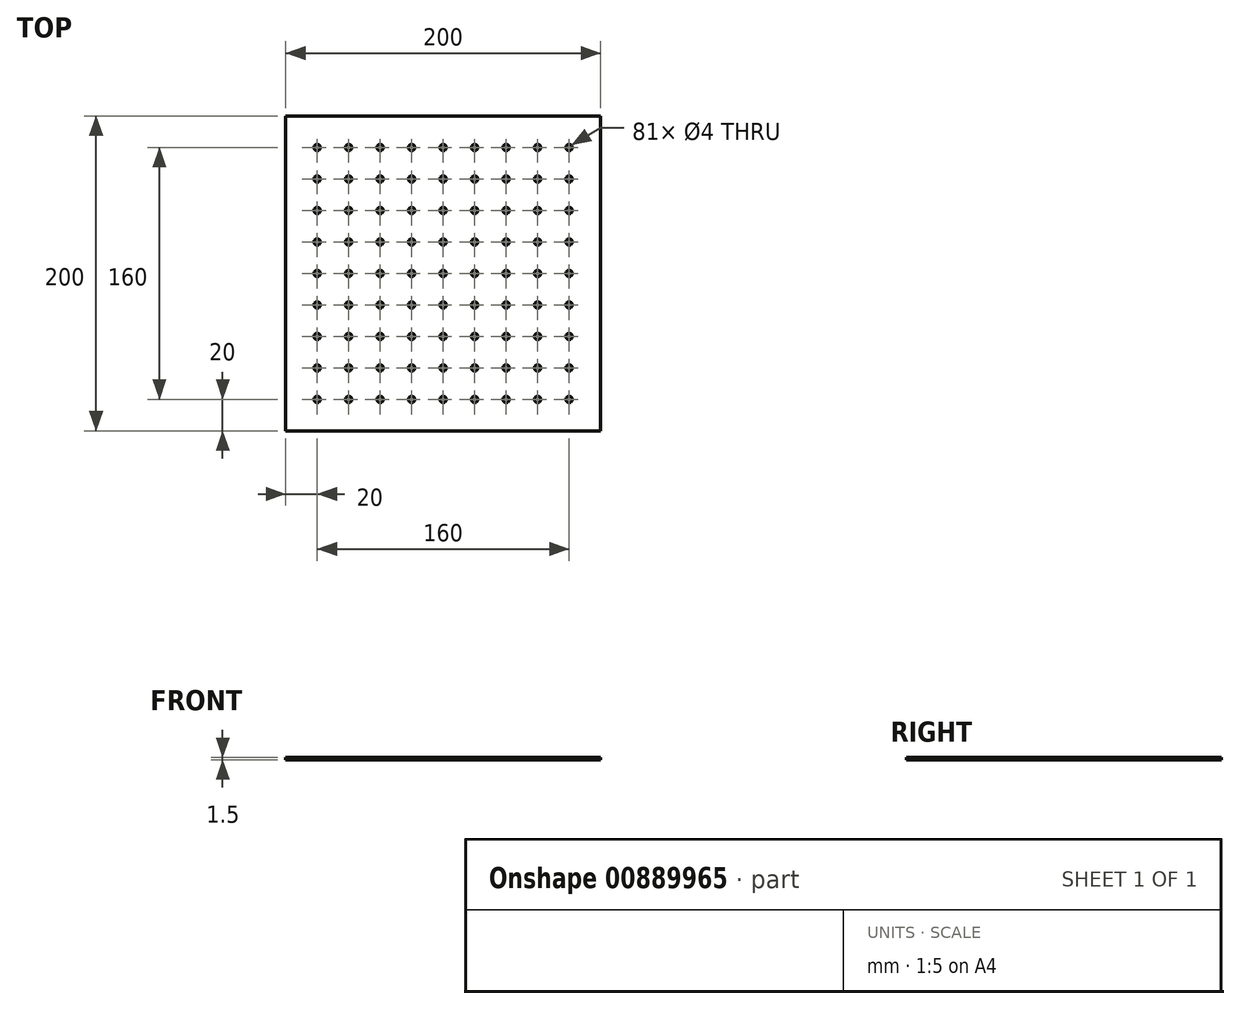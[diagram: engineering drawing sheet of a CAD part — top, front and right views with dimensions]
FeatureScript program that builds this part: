
annotation { "Feature Type Name" : "Feature", "Feature Type Description" : "" }
export const myFeature = defineFeature(function(context is Context, id is Id, definition is map)
    precondition{}
    {
        {
            var Q0;
            Q0=qCreatedBy(makeId("Top.planeOp"),FACE);
            var sketch = newSketch(context, id + "F0", { "sketchPlane" : qUnion([Q0])});
            skLineSegment(sketch, "E0.bottom", {"start": v(-100, 100) * mm, "end": v(100, 100) * mm});
            skLineSegment(sketch, "E0.top", {"start": v(-100, -100) * mm, "end": v(100, -100) * mm});
            skLineSegment(sketch, "E0.left", {"start": v(-100, 100) * mm, "end": v(-100, -100) * mm});
            skLineSegment(sketch, "E0.right", {"start": v(100, 100) * mm, "end": v(100, -100) * mm});
            skPoint(sketch, "E0.middle", {"position": v(0, 0) * mm});
            skCircle(sketch, "E1", {"center": v(-80, -80) * mm, "radius": 2 * mm});
            skCircle(sketch, "E2.0.1.0", {"center": v(-80, -60) * mm, "radius": 2 * mm});
            skCircle(sketch, "E2.0.2.0", {"center": v(-80, -40) * mm, "radius": 2 * mm});
            skCircle(sketch, "E2.0.3.0", {"center": v(-80, -20) * mm, "radius": 2 * mm});
            skCircle(sketch, "E2.0.4.0", {"center": v(-80, 0) * mm, "radius": 2 * mm});
            skCircle(sketch, "E2.0.5.0", {"center": v(-80, 20) * mm, "radius": 2 * mm});
            skCircle(sketch, "E2.0.6.0", {"center": v(-80, 40) * mm, "radius": 2 * mm});
            skCircle(sketch, "E2.0.7.0", {"center": v(-80, 60) * mm, "radius": 2 * mm});
            skCircle(sketch, "E2.0.8.0", {"center": v(-80, 80) * mm, "radius": 2 * mm});
            skCircle(sketch, "E2.1.0.0", {"center": v(-60, -80) * mm, "radius": 2 * mm});
            skCircle(sketch, "E2.1.1.0", {"center": v(-60, -60) * mm, "radius": 2 * mm});
            skCircle(sketch, "E2.1.2.0", {"center": v(-60, -40) * mm, "radius": 2 * mm});
            skCircle(sketch, "E2.1.3.0", {"center": v(-60, -20) * mm, "radius": 2 * mm});
            skCircle(sketch, "E2.1.4.0", {"center": v(-60, 0) * mm, "radius": 2 * mm});
            skCircle(sketch, "E2.1.5.0", {"center": v(-60, 20) * mm, "radius": 2 * mm});
            skCircle(sketch, "E2.1.6.0", {"center": v(-60, 40) * mm, "radius": 2 * mm});
            skCircle(sketch, "E2.1.7.0", {"center": v(-60, 60) * mm, "radius": 2 * mm});
            skCircle(sketch, "E2.1.8.0", {"center": v(-60, 80) * mm, "radius": 2 * mm});
            skCircle(sketch, "E2.2.0.0", {"center": v(-40, -80) * mm, "radius": 2 * mm});
            skCircle(sketch, "E2.2.1.0", {"center": v(-40, -60) * mm, "radius": 2 * mm});
            skCircle(sketch, "E2.2.2.0", {"center": v(-40, -40) * mm, "radius": 2 * mm});
            skCircle(sketch, "E2.2.3.0", {"center": v(-40, -20) * mm, "radius": 2 * mm});
            skCircle(sketch, "E2.2.4.0", {"center": v(-40, 0) * mm, "radius": 2 * mm});
            skCircle(sketch, "E2.2.5.0", {"center": v(-40, 20) * mm, "radius": 2 * mm});
            skCircle(sketch, "E2.2.6.0", {"center": v(-40, 40) * mm, "radius": 2 * mm});
            skCircle(sketch, "E2.2.7.0", {"center": v(-40, 60) * mm, "radius": 2 * mm});
            skCircle(sketch, "E2.2.8.0", {"center": v(-40, 80) * mm, "radius": 2 * mm});
            skCircle(sketch, "E2.3.0.0", {"center": v(-20, -80) * mm, "radius": 2 * mm});
            skCircle(sketch, "E2.3.1.0", {"center": v(-20, -60) * mm, "radius": 2 * mm});
            skCircle(sketch, "E2.3.2.0", {"center": v(-20, -40) * mm, "radius": 2 * mm});
            skCircle(sketch, "E2.3.3.0", {"center": v(-20, -20) * mm, "radius": 2 * mm});
            skCircle(sketch, "E2.3.4.0", {"center": v(-20, 0) * mm, "radius": 2 * mm});
            skCircle(sketch, "E2.3.5.0", {"center": v(-20, 20) * mm, "radius": 2 * mm});
            skCircle(sketch, "E2.3.6.0", {"center": v(-20, 40) * mm, "radius": 2 * mm});
            skCircle(sketch, "E2.3.7.0", {"center": v(-20, 60) * mm, "radius": 2 * mm});
            skCircle(sketch, "E2.3.8.0", {"center": v(-20, 80) * mm, "radius": 2 * mm});
            skCircle(sketch, "E2.4.0.0", {"center": v(0, -80) * mm, "radius": 2 * mm});
            skCircle(sketch, "E2.4.1.0", {"center": v(0, -60) * mm, "radius": 2 * mm});
            skCircle(sketch, "E2.4.2.0", {"center": v(0, -40) * mm, "radius": 2 * mm});
            skCircle(sketch, "E2.4.3.0", {"center": v(0, -20) * mm, "radius": 2 * mm});
            skCircle(sketch, "E2.4.4.0", {"center": v(0, 0) * mm, "radius": 2 * mm});
            skCircle(sketch, "E2.4.5.0", {"center": v(0, 20) * mm, "radius": 2 * mm});
            skCircle(sketch, "E2.4.6.0", {"center": v(0, 40) * mm, "radius": 2 * mm});
            skCircle(sketch, "E2.4.7.0", {"center": v(0, 60) * mm, "radius": 2 * mm});
            skCircle(sketch, "E2.4.8.0", {"center": v(0, 80) * mm, "radius": 2 * mm});
            skCircle(sketch, "E2.5.0.0", {"center": v(20, -80) * mm, "radius": 2 * mm});
            skCircle(sketch, "E2.5.1.0", {"center": v(20, -60) * mm, "radius": 2 * mm});
            skCircle(sketch, "E2.5.2.0", {"center": v(20, -40) * mm, "radius": 2 * mm});
            skCircle(sketch, "E2.5.3.0", {"center": v(20, -20) * mm, "radius": 2 * mm});
            skCircle(sketch, "E2.5.4.0", {"center": v(20, 0) * mm, "radius": 2 * mm});
            skCircle(sketch, "E2.5.5.0", {"center": v(20, 20) * mm, "radius": 2 * mm});
            skCircle(sketch, "E2.5.6.0", {"center": v(20, 40) * mm, "radius": 2 * mm});
            skCircle(sketch, "E2.5.7.0", {"center": v(20, 60) * mm, "radius": 2 * mm});
            skCircle(sketch, "E2.5.8.0", {"center": v(20, 80) * mm, "radius": 2 * mm});
            skCircle(sketch, "E2.6.0.0", {"center": v(40, -80) * mm, "radius": 2 * mm});
            skCircle(sketch, "E2.6.1.0", {"center": v(40, -60) * mm, "radius": 2 * mm});
            skCircle(sketch, "E2.6.2.0", {"center": v(40, -40) * mm, "radius": 2 * mm});
            skCircle(sketch, "E2.6.3.0", {"center": v(40, -20) * mm, "radius": 2 * mm});
            skCircle(sketch, "E2.6.4.0", {"center": v(40, 0) * mm, "radius": 2 * mm});
            skCircle(sketch, "E2.6.5.0", {"center": v(40, 20) * mm, "radius": 2 * mm});
            skCircle(sketch, "E2.6.6.0", {"center": v(40, 40) * mm, "radius": 2 * mm});
            skCircle(sketch, "E2.6.7.0", {"center": v(40, 60) * mm, "radius": 2 * mm});
            skCircle(sketch, "E2.6.8.0", {"center": v(40, 80) * mm, "radius": 2 * mm});
            skCircle(sketch, "E2.7.0.0", {"center": v(60, -80) * mm, "radius": 2 * mm});
            skCircle(sketch, "E2.7.1.0", {"center": v(60, -60) * mm, "radius": 2 * mm});
            skCircle(sketch, "E2.7.2.0", {"center": v(60, -40) * mm, "radius": 2 * mm});
            skCircle(sketch, "E2.7.3.0", {"center": v(60, -20) * mm, "radius": 2 * mm});
            skCircle(sketch, "E2.7.4.0", {"center": v(60, 0) * mm, "radius": 2 * mm});
            skCircle(sketch, "E2.7.5.0", {"center": v(60, 20) * mm, "radius": 2 * mm});
            skCircle(sketch, "E2.7.6.0", {"center": v(60, 40) * mm, "radius": 2 * mm});
            skCircle(sketch, "E2.7.7.0", {"center": v(60, 60) * mm, "radius": 2 * mm});
            skCircle(sketch, "E2.7.8.0", {"center": v(60, 80) * mm, "radius": 2 * mm});
            skCircle(sketch, "E2.8.0.0", {"center": v(80, -80) * mm, "radius": 2 * mm});
            skCircle(sketch, "E2.8.1.0", {"center": v(80, -60) * mm, "radius": 2 * mm});
            skCircle(sketch, "E2.8.2.0", {"center": v(80, -40) * mm, "radius": 2 * mm});
            skCircle(sketch, "E2.8.3.0", {"center": v(80, -20) * mm, "radius": 2 * mm});
            skCircle(sketch, "E2.8.4.0", {"center": v(80, 0) * mm, "radius": 2 * mm});
            skCircle(sketch, "E2.8.5.0", {"center": v(80, 20) * mm, "radius": 2 * mm});
            skCircle(sketch, "E2.8.6.0", {"center": v(80, 40) * mm, "radius": 2 * mm});
            skCircle(sketch, "E2.8.7.0", {"center": v(80, 60) * mm, "radius": 2 * mm});
            skCircle(sketch, "E2.8.8.0", {"center": v(80, 80) * mm, "radius": 2 * mm});
            skLineSegment(sketch, "E2.direction1", {"start": v(-80, -80) * mm, "end": v(-60, -80) * mm, "construction": true});
            skLineSegment(sketch, "E2.direction2", {"start": v(-80, -80) * mm, "end": v(-80, -60) * mm, "construction": true});
            skSolve(sketch);
        }
        {
            var Q0;
            Q0 = qSketchRegion(id + "F0", true);
            extrude(context, id + "F1", {"entities" : qUnion([Q0]), "depth" : 1.5 * mm, "offsetDistance" : 25 * mm});
        }
    });
